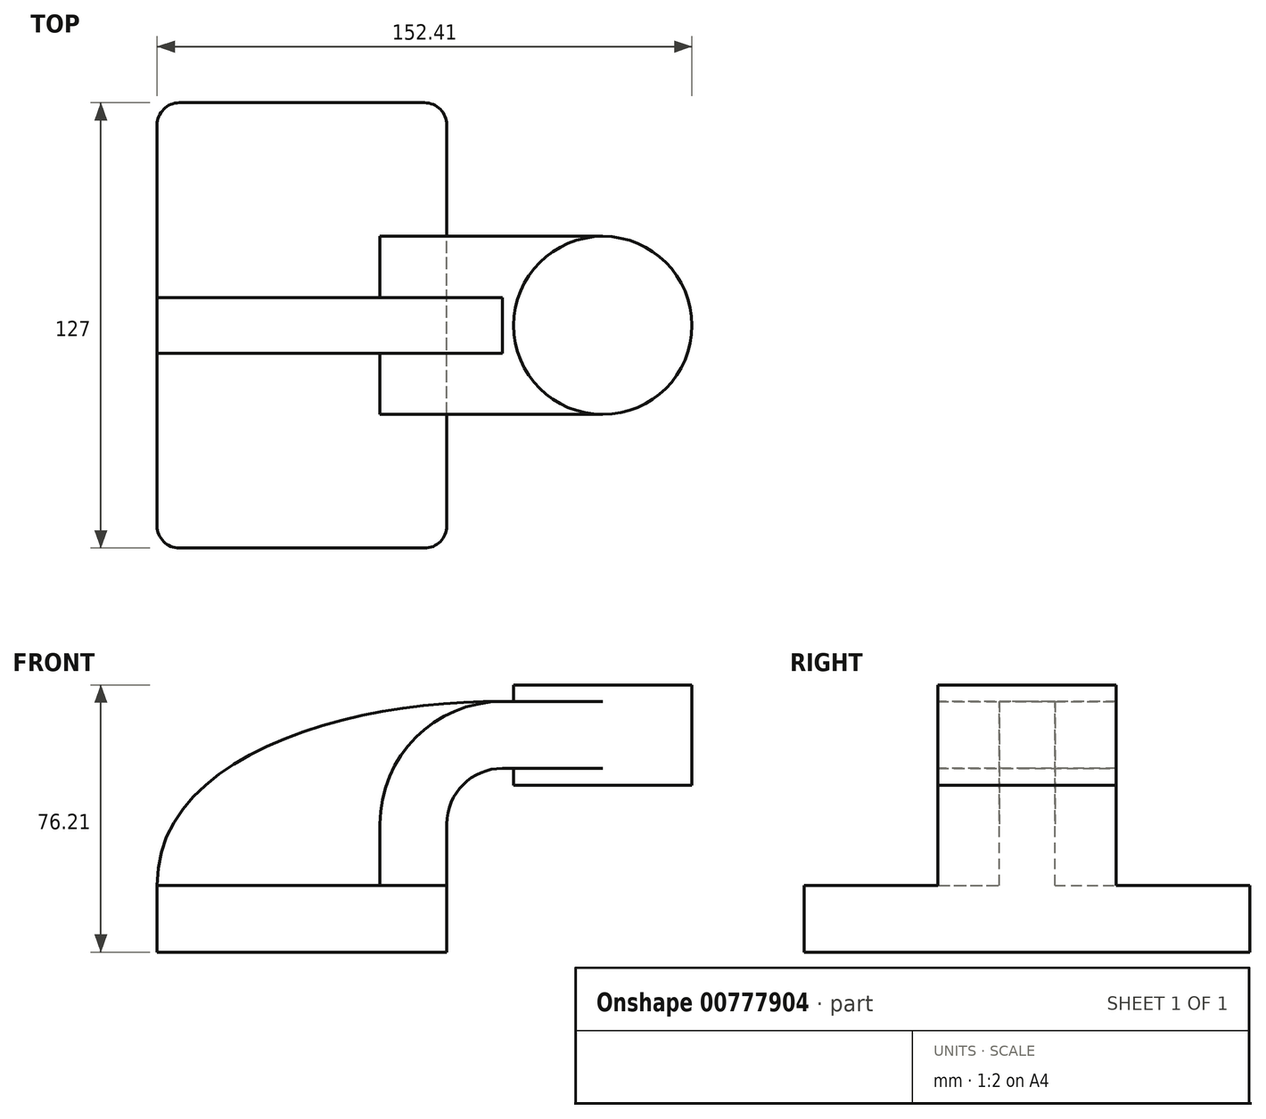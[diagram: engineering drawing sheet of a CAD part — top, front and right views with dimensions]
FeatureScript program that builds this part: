
annotation { "Feature Type Name" : "Feature", "Feature Type Description" : "" }
export const myFeature = defineFeature(function(context is Context, id is Id, definition is map)
    precondition{}
    {
        {
            var Q0;
            Q0=qCreatedBy(makeId("Front.planeOp"),FACE);
            var sketch = newSketch(context, id + "F0", { "sketchPlane" : qUnion([Q0])});
            skLineSegment(sketch, "E0.bottom", {"start": v(-41.28, -9.53) * mm, "end": v(41.28, -9.53) * mm});
            skLineSegment(sketch, "E0.top", {"start": v(-41.28, 9.52) * mm, "end": v(41.28, 9.52) * mm});
            skLineSegment(sketch, "E0.left", {"start": v(-41.28, -9.53) * mm, "end": v(-41.28, 9.52) * mm});
            skLineSegment(sketch, "E0.right", {"start": v(41.28, -9.53) * mm, "end": v(41.28, 9.52) * mm});
            skPoint(sketch, "E0.middle", {"position": v(0, 0) * mm});
            skLineSegment(sketch, "E1.bottom", {"start": v(60.33, 38.1) * mm, "end": v(111.13, 38.1) * mm});
            skLineSegment(sketch, "E1.top", {"start": v(60.33, 66.67) * mm, "end": v(111.13, 66.67) * mm});
            skLineSegment(sketch, "E1.left", {"start": v(60.33, 38.1) * mm, "end": v(60.33, 66.68) * mm});
            skLineSegment(sketch, "E1.right", {"start": v(111.13, 38.1) * mm, "end": v(111.13, 66.68) * mm});
            skPoint(sketch, "E1.middle", {"position": v(85.73, 52.39) * mm});
            skLineSegment(sketch, "E2", {"start": v(41.27, 9.52) * mm, "end": v(41.27, 27) * mm});
            skArc(sketch, "E3", {"start": v(41.27, 27) * mm, "mid": v(45.92, 38.23) * mm, "end": v(57.15, 42.88) * mm});
            skFitSpline(sketch, "E4", {"points": [v(-41.28, 9.52) * mm, v(57.15, 61.93) * mm], "startDerivative": vector(-0.72, 114.44) * mm, "endDerivative": vector(123.22, -1.68) * mm});
            skLineSegment(sketch, "E5", {"start": v(57.15, 42.88) * mm, "end": v(85.73, 42.88) * mm});
            skLineSegment(sketch, "E6.0", {"start": v(57.15, 61.93) * mm, "end": v(85.73, 61.93) * mm});
            skArc(sketch, "E6.1", {"start": v(22.22, 27) * mm, "mid": v(32.45, 51.7) * mm, "end": v(57.15, 61.93) * mm});
            skLineSegment(sketch, "E6.2", {"start": v(22.23, 9.52) * mm, "end": v(22.23, 27) * mm});
            skPoint(sketch, "E7", {"position": v(85.73, 66.67) * mm});
            skPoint(sketch, "E8", {"position": v(85.73, 38.1) * mm});
            skLineSegment(sketch, "E9", {"start": v(85.73, 38.1) * mm, "end": v(85.73, 66.67) * mm});
            skSolve(sketch);
        }
        {
            var Q0;
            Q0=makeQuery(id+"F0.imprint","IMPRINT",FACE,{"disambiguationData":[TD([[makeQuery(id+"F0.imprint","IMPRINT",EDGE,{"derivedFrom":sQuery(id+"F0.wireOp",EDGE,"E0.bottom")}),1.0]])]});
            extrude(context, id + "F1", {"entities" : qUnion([Q0]), "endBound" : BoundingType.SYMMETRIC, "depth" : 127 * mm, "offsetDistance" : 25.4 * mm});
        }
        {
            var Q0;
            {var subQ1=sQuery(id+"F0.wireOp",EDGE,"E2");Q0=makeQuery(id+"F0.imprint","IMPRINT",FACE,{"disambiguationData":[TD([[makeQuery(id+"F0.imprint","IMPRINT",EDGE,{"derivedFrom":subQ1}),1.0]])]});}
            var Q1;
            {var subQ0=sQuery(id+"F0.wireOp",EDGE,"E5");var subQ1=sQuery(id+"F0.wireOp",EDGE,"E1.left");var subQ2=makeQuery(id+"F0.imprint","INTERSECT",VERTEX,{"derivedFrom":[subQ1,subQ0]});Q1=makeQuery(id+"F0.imprint","IMPRINT",FACE,{"disambiguationData":[TD([[makeQuery(id+"F0.imprint","IMPRINT",EDGE,{"disambiguationData":[TD([[subQ2,-1.0]])],"derivedFrom":subQ1}),-1.0]])]});}
            extrude(context, id + "F2", {"entities" : qUnion([Q0, Q1]), "operationType" : NewBodyOperationType.ADD, "endBound" : BoundingType.SYMMETRIC, "depth" : 50.8 * mm, "offsetDistance" : 25.4 * mm});
        }
        {
            var Q0;
            Q0=makeQuery(id+"F0.imprint","IMPRINT",FACE,{"disambiguationData":[TD([[makeQuery(id+"F0.imprint","IMPRINT",EDGE,{"derivedFrom":sQuery(id+"F0.wireOp",EDGE,"862901ed-ce48-440d-8f73-f7f9e67912f5.1")}),1.0]])]});
            var Q1;
            {var subQ0=sQuery(id+"F0.wireOp",EDGE,"E4");Q1=makeQuery(id+"F0.imprint","IMPRINT",FACE,{"disambiguationData":[TD([[makeQuery(id+"F0.imprint","IMPRINT",EDGE,{"derivedFrom":subQ0}),-1.0]])]});}
            extrude(context, id + "F3", {"entities" : qUnion([Q0, Q1]), "operationType" : NewBodyOperationType.ADD, "endBound" : BoundingType.SYMMETRIC, "depth" : 15.88 * mm, "offsetDistance" : 25.4 * mm});
        }
        {
            var Q0;
            {var subQ4=sQuery(id+"F0.wireOp",EDGE,"E1.right");Q0=makeQuery(id+"F0.imprint","IMPRINT",FACE,{"disambiguationData":[TD([[makeQuery(id+"F0.imprint","IMPRINT",EDGE,{"derivedFrom":subQ4}),1.0]])]});}
            var Q1;
            Q1=sQuery(id+"F0.wireOp",EDGE,"E9");
            revolve(context, id + "F4", {"operationType" : NewBodyOperationType.ADD, "surfaceOperationType" : NewSurfaceOperationType.NEW, "entities" : qUnion([Q0]), "axis" : qUnion([Q1]), "revolveType" : RevolveType.FULL});
        }
        {
            var Q0;
            Q0=makeQuery(id+"F1.opExtrude","CAP_EDGE",EDGE,{"disambiguationData":[OSD([sQuery(id+"F0.wireOp",EDGE,"E0.left")])],"isStart":false});
            var Q1;
            Q1=makeQuery(id+"F1.opExtrude","CAP_EDGE",EDGE,{"disambiguationData":[OSD([sQuery(id+"F0.wireOp",EDGE,"E0.right")])],"isStart":false});
            var Q2;
            Q2=makeQuery(id+"F1.opExtrude","CAP_EDGE",EDGE,{"disambiguationData":[OSD([sQuery(id+"F0.wireOp",EDGE,"E0.right")])],"isStart":true});
            var Q3;
            Q3=makeQuery(id+"F1.opExtrude","CAP_EDGE",EDGE,{"disambiguationData":[OSD([sQuery(id+"F0.wireOp",EDGE,"E0.left")])],"isStart":true});
            fillet(context, id + "F5", {"entities" : qUnion([Q0, Q1, Q2, Q3]), "radius" : 6.35 * mm, "tangentPropagation" : true, "allowEdgeOverflow" : false});
        }
    });
